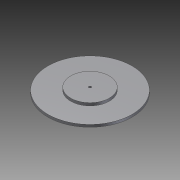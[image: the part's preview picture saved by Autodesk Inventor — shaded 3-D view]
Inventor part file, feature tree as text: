
AUTODESK INVENTOR PART (.ipt)
format: ipt  version: 2011 (Build 150239000, 239)  size: 80,384 bytes
history: native  units: mm
features: extrude x2, sketch x2, other x1
ambient origin geometry x8: Origin, YZ Plane, XZ Plane, XY Plane, X Axis, Y Axis, Z Axis, Center Point
feature tree (5):
  other  "Sólido1"
  extrude  "Extrusión1"  Depth=1.0mm
  extrude  "Extrusión2"  Depth=15.6mm
  sketch  "Boceto1"  dims[d0=34.0mm d1=1.0mm]
  sketch  "Boceto2"  dims[d2=1.0mm d3=0.0mm d4=15.6mm d5=1.1mm d6=0.0mm]
